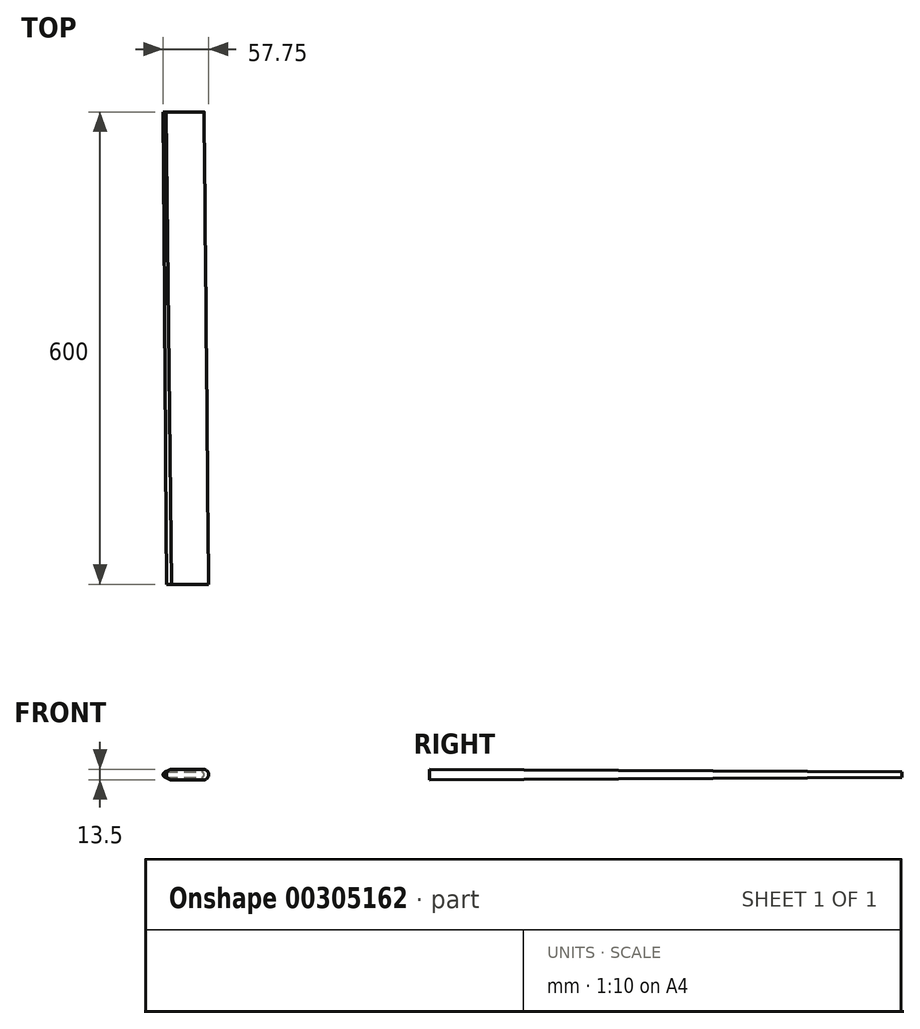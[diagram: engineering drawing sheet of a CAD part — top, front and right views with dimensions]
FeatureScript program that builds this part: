
annotation { "Feature Type Name" : "Feature", "Feature Type Description" : "" }
export const myFeature = defineFeature(function(context is Context, id is Id, definition is map)
    precondition{}
    {
        {
            var Q0;
            Q0=qCreatedBy(makeId("Front.planeOp"),FACE);
            var sketch = newSketch(context, id + "F0", { "sketchPlane" : qUnion([Q0])});
            skLineSegment(sketch, "E0.bottom", {"start": v(-20, 3.25) * mm, "end": v(20, 3.25) * mm, "construction": true});
            skLineSegment(sketch, "E0.top", {"start": v(-20, -3.25) * mm, "end": v(20, -3.25) * mm, "construction": true});
            skPoint(sketch, "E0.middle", {"position": v(0, 0) * mm});
            skArc(sketch, "E1", {"start": v(-20, 3.25) * mm, "mid": v(-23.25, 0) * mm, "end": v(-20, -3.25) * mm, "construction": true});
            skArc(sketch, "E2", {"start": v(20, -3.25) * mm, "mid": v(23.25, 0) * mm, "end": v(20, 3.25) * mm, "construction": true});
            skLineSegment(sketch, "E3.0", {"start": v(-20, 6.75) * mm, "end": v(20, 6.75) * mm});
            skArc(sketch, "E3.1", {"start": v(-20, 6.75) * mm, "mid": v(-26.75, 0) * mm, "end": v(-20, -6.75) * mm});
            skLineSegment(sketch, "E3.2", {"start": v(-20, -6.75) * mm, "end": v(20, -6.75) * mm});
            skArc(sketch, "E3.3", {"start": v(20, -6.75) * mm, "mid": v(26.75, 0) * mm, "end": v(20, 6.75) * mm});
            skSolve(sketch);
        }
        {
            var Q0;
            Q0=qCreatedBy(makeId("Front.planeOp"),FACE);
            cPlane(context, id + "F1", {"entities" : qUnion([Q0]), "cplaneType" : CPlaneType.OFFSET, "offset" : 600 * mm, "oppositeDirection" : true, "width" : 150 * mm, "height" : 150 * mm});
        }
        {
            var Q0;
            Q0=qCreatedBy(id+"F1.planeOp",FACE);
            var sketch = newSketch(context, id + "F2", { "sketchPlane" : qUnion([Q0])});
            skLineSegment(sketch, "E4.bottom", {"start": v(-27.5, 3.5) * mm, "end": v(17.5, 3.5) * mm});
            skLineSegment(sketch, "E4.top", {"start": v(-27.5, -3.5) * mm, "end": v(17.5, -3.5) * mm});
            skPoint(sketch, "E4.middle", {"position": v(-5, 0) * mm});
            skArc(sketch, "E5", {"start": v(-27.5, 3.5) * mm, "mid": v(-31, 0) * mm, "end": v(-27.5, -3.5) * mm});
            skArc(sketch, "E6", {"start": v(17.5, -3.5) * mm, "mid": v(21, 0) * mm, "end": v(17.5, 3.5) * mm});
            skLineSegment(sketch, "E7.0", {"start": v(-27.5, 0) * mm, "end": v(17.5, 0) * mm, "construction": true});
            skLineSegment(sketch, "E7.1", {"start": v(-27.5, 0) * mm, "end": v(-27.5, 0) * mm});
            skLineSegment(sketch, "E7.2", {"start": v(-27.5, 0) * mm, "end": v(17.5, 0) * mm, "construction": true});
            skLineSegment(sketch, "E7.3", {"start": v(17.5, 0) * mm, "end": v(17.5, 0) * mm});
            skSolve(sketch);
        }
        {
            var Q0;
            Q0=makeQuery(id+"F2.imprint","IMPRINT",FACE,{"disambiguationData":[TD([[makeQuery(id+"F2.imprint","IMPRINT",EDGE,{"derivedFrom":sQuery(id+"F2.wireOp",EDGE,"E4.bottom")}),-1.0]])]});
            var Q1;
            Q1=makeQuery(id+"F0.imprint","IMPRINT",FACE,{"disambiguationData":[TD([[makeQuery(id+"F0.imprint","IMPRINT",EDGE,{"derivedFrom":sQuery(id+"F0.wireOp",EDGE,"E3.0")}),-1.0]])]});
            loft(context, id + "F3", {"sheetProfilesArray" : [{ "sheetProfileEntities" : qUnion([Q0]) }, { "sheetProfileEntities" : qUnion([Q1]) }]});
        }
    });
